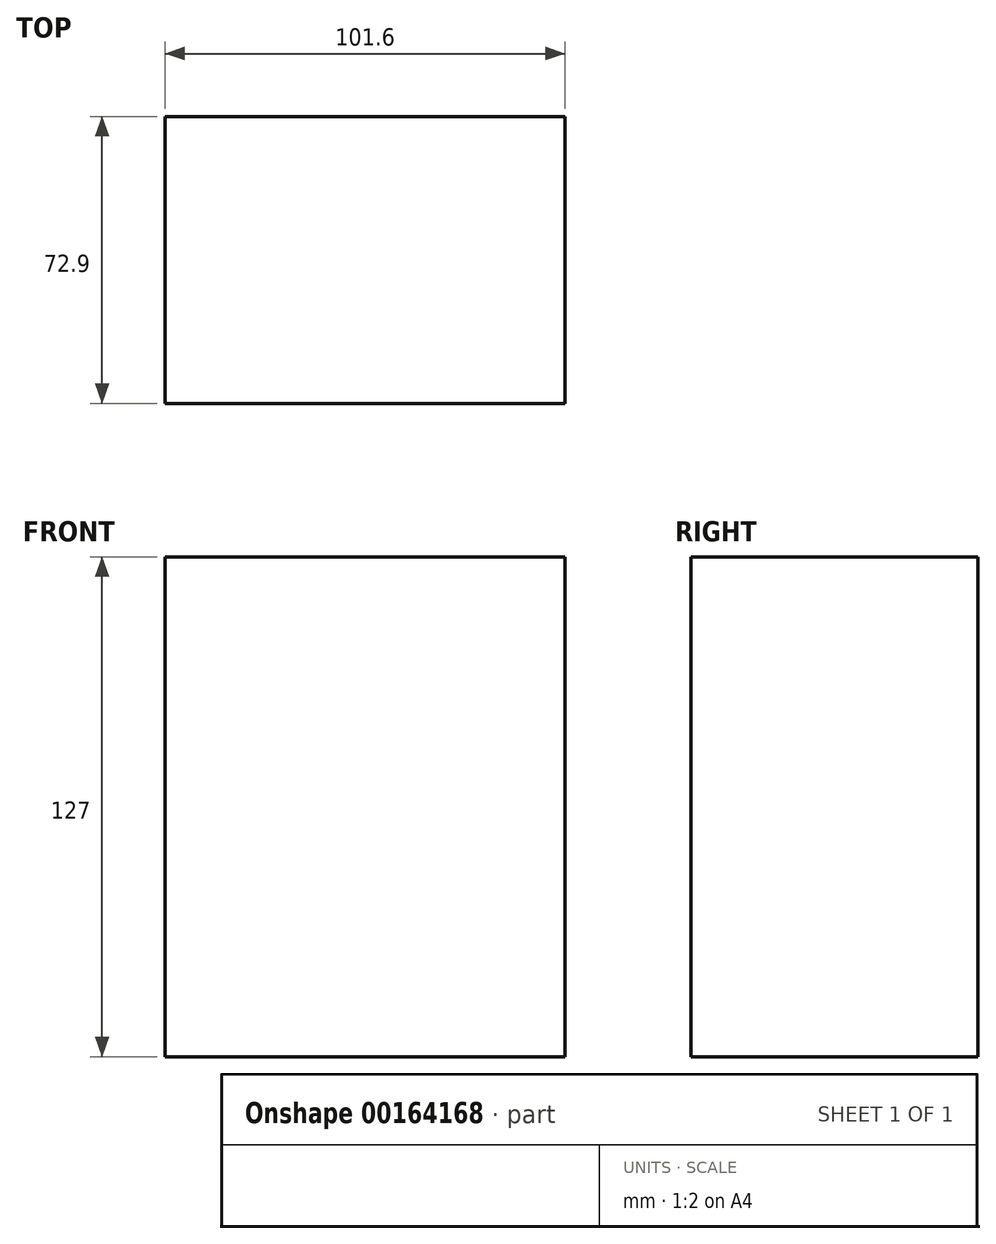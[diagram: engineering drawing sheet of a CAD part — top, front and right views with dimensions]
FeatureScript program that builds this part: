
annotation { "Feature Type Name" : "Feature", "Feature Type Description" : "" }
export const myFeature = defineFeature(function(context is Context, id is Id, definition is map)
    precondition{}
    {
        {
            var Q0;
            Q0=qCreatedBy(makeId("Front.planeOp"),FACE);
            var sketch = newSketch(context, id + "F0", { "sketchPlane" : qUnion([Q0])});
            skLineSegment(sketch, "E0.bottom", {"start": v(0, 0) * mm, "end": v(101.6, 0) * mm});
            skLineSegment(sketch, "E0.top", {"start": v(0, 127) * mm, "end": v(101.6, 127) * mm});
            skLineSegment(sketch, "E0.left", {"start": v(0, 0) * mm, "end": v(0, 127) * mm});
            skLineSegment(sketch, "E0.right", {"start": v(101.6, 0) * mm, "end": v(101.6, 127) * mm});
            skSolve(sketch);
        }
        {
            var Q0;
            Q0=makeQuery(id+"F0.imprint","IMPRINT",FACE,{"disambiguationData":[TD([[makeQuery(id+"F0.imprint","IMPRINT",EDGE,{"derivedFrom":sQuery(id+"F0.wireOp",EDGE,"E0.bottom")}),1.0]])]});
            extrude(context, id + "F1", {"entities" : qUnion([Q0]), "depth" : 72.9 * mm});
        }
    });
